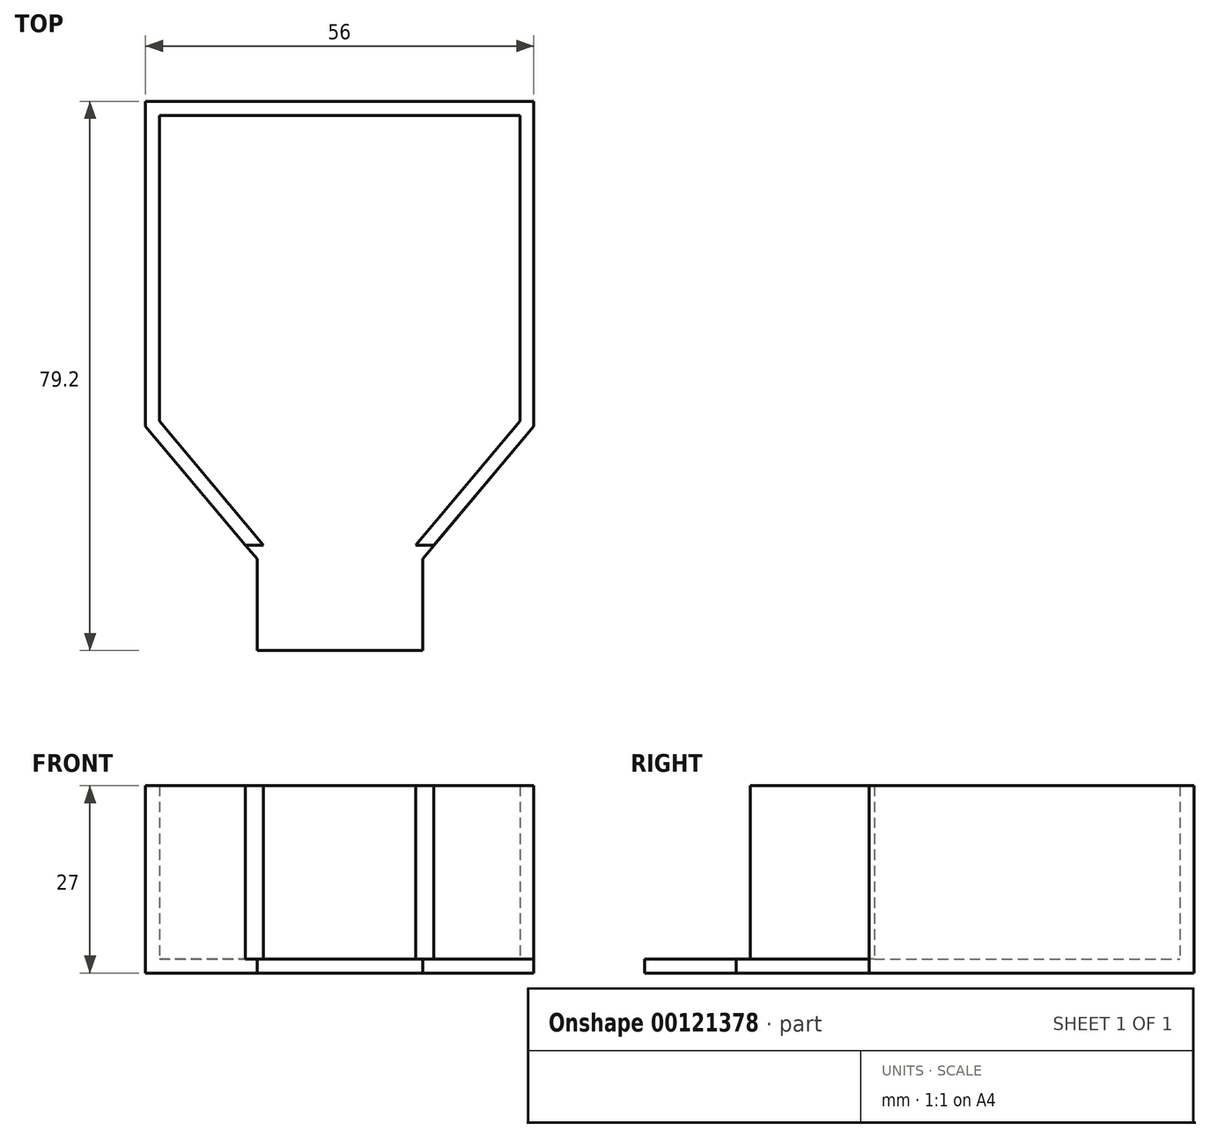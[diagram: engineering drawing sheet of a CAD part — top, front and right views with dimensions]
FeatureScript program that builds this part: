
annotation { "Feature Type Name" : "Feature", "Feature Type Description" : "" }
export const myFeature = defineFeature(function(context is Context, id is Id, definition is map)
    precondition{}
    {
        {
            var Q0;
            Q0=qCreatedBy(makeId("Top.planeOp"),FACE);
            var sketch = newSketch(context, id + "F0", { "sketchPlane" : qUnion([Q0])});
            skLineSegment(sketch, "E0.top", {"start": v(26, 31) * mm, "end": v(-26, 31) * mm});
            skPoint(sketch, "E0.middle", {"position": v(0, 0) * mm});
            skLineSegment(sketch, "E1", {"start": v(-26, -13.1) * mm, "end": v(-10.98, -31) * mm});
            skLineSegment(sketch, "E2", {"start": v(26, -13.1) * mm, "end": v(10.98, -31) * mm});
            skLineSegment(sketch, "E3.0", {"start": v(28, -13.83) * mm, "end": v(28, 33) * mm});
            skLineSegment(sketch, "E4.0", {"start": v(28, 33) * mm, "end": v(-28, 33) * mm});
            skLineSegment(sketch, "E5.0", {"start": v(-28, -13.83) * mm, "end": v(-28, 33) * mm});
            skLineSegment(sketch, "E6.0", {"start": v(-28, -13.83) * mm, "end": v(-13.6, -31) * mm});
            skLineSegment(sketch, "E7.0", {"start": v(28, -13.83) * mm, "end": v(13.6, -31) * mm});
            skLineSegment(sketch, "E8.trimOffspring", {"start": v(-26, -13.1) * mm, "end": v(-26, 31) * mm});
            skLineSegment(sketch, "E9.trimOffspring", {"start": v(26, -13.1) * mm, "end": v(26, 31) * mm});
            skLineSegment(sketch, "E10", {"start": v(-13.6, -31) * mm, "end": v(-10.98, -31) * mm});
            skLineSegment(sketch, "E11", {"start": v(10.98, -31) * mm, "end": v(13.6, -31) * mm});
            skSolve(sketch);
        }
        {
            var Q0;
            Q0 = qSketchRegion(id + "F0", true);
            extrude(context, id + "F1", {"entities" : qUnion([Q0]), "depth" : 25 * mm});
        }
        {
            var Q0;
            Q0=makeQuery(id+"F1.opExtrude","CAP_FACE",FACE,{"disambiguationData":[OSD([sQuery(id+"F0.wireOp",EDGE,"E0.top"),sQuery(id+"F0.wireOp",EDGE,"E1"),sQuery(id+"F0.wireOp",EDGE,"E2"),sQuery(id+"F0.wireOp",EDGE,"E3.0"),sQuery(id+"F0.wireOp",EDGE,"E4.0"),sQuery(id+"F0.wireOp",EDGE,"E5.0"),sQuery(id+"F0.wireOp",EDGE,"E6.0"),sQuery(id+"F0.wireOp",EDGE,"E7.0"),sQuery(id+"F0.wireOp",EDGE,"E8.trimOffspring"),sQuery(id+"F0.wireOp",EDGE,"E9.trimOffspring"),sQuery(id+"F0.wireOp",EDGE,"E10"),sQuery(id+"F0.wireOp",EDGE,"E11")])],"isStart":true});
            var sketch = newSketch(context, id + "F2", { "sketchPlane" : qUnion([Q0])});
            skLineSegment(sketch, "E12.bottom", {"start": v(28, -33) * mm, "end": v(-28, -33) * mm});
            skLineSegment(sketch, "E12.left", {"start": v(28, -33) * mm, "end": v(28, 13.83) * mm});
            skLineSegment(sketch, "E12.right", {"start": v(-28, -33) * mm, "end": v(-28, 13.83) * mm});
            skPoint(sketch, "E12.middle", {"position": v(0, 0) * mm});
            skLineSegment(sketch, "E13", {"start": v(-28, 13.83) * mm, "end": v(-11.92, 33) * mm});
            skLineSegment(sketch, "E14", {"start": v(28, 13.83) * mm, "end": v(12, 33) * mm});
            skLineSegment(sketch, "E15", {"start": v(-11.92, 33) * mm, "end": v(-11.92, 46.2) * mm});
            skLineSegment(sketch, "E16", {"start": v(-11.92, 46.2) * mm, "end": v(12, 46.2) * mm});
            skLineSegment(sketch, "E17", {"start": v(12, 46.2) * mm, "end": v(12, 33) * mm});
            skSolve(sketch);
        }
        {
            var Q0;
            Q0 = qSketchRegion(id + "F2", true);
            extrude(context, id + "F3", {"entities" : qUnion([Q0]), "operationType" : NewBodyOperationType.ADD, "depth" : 2 * mm});
        }
    });
